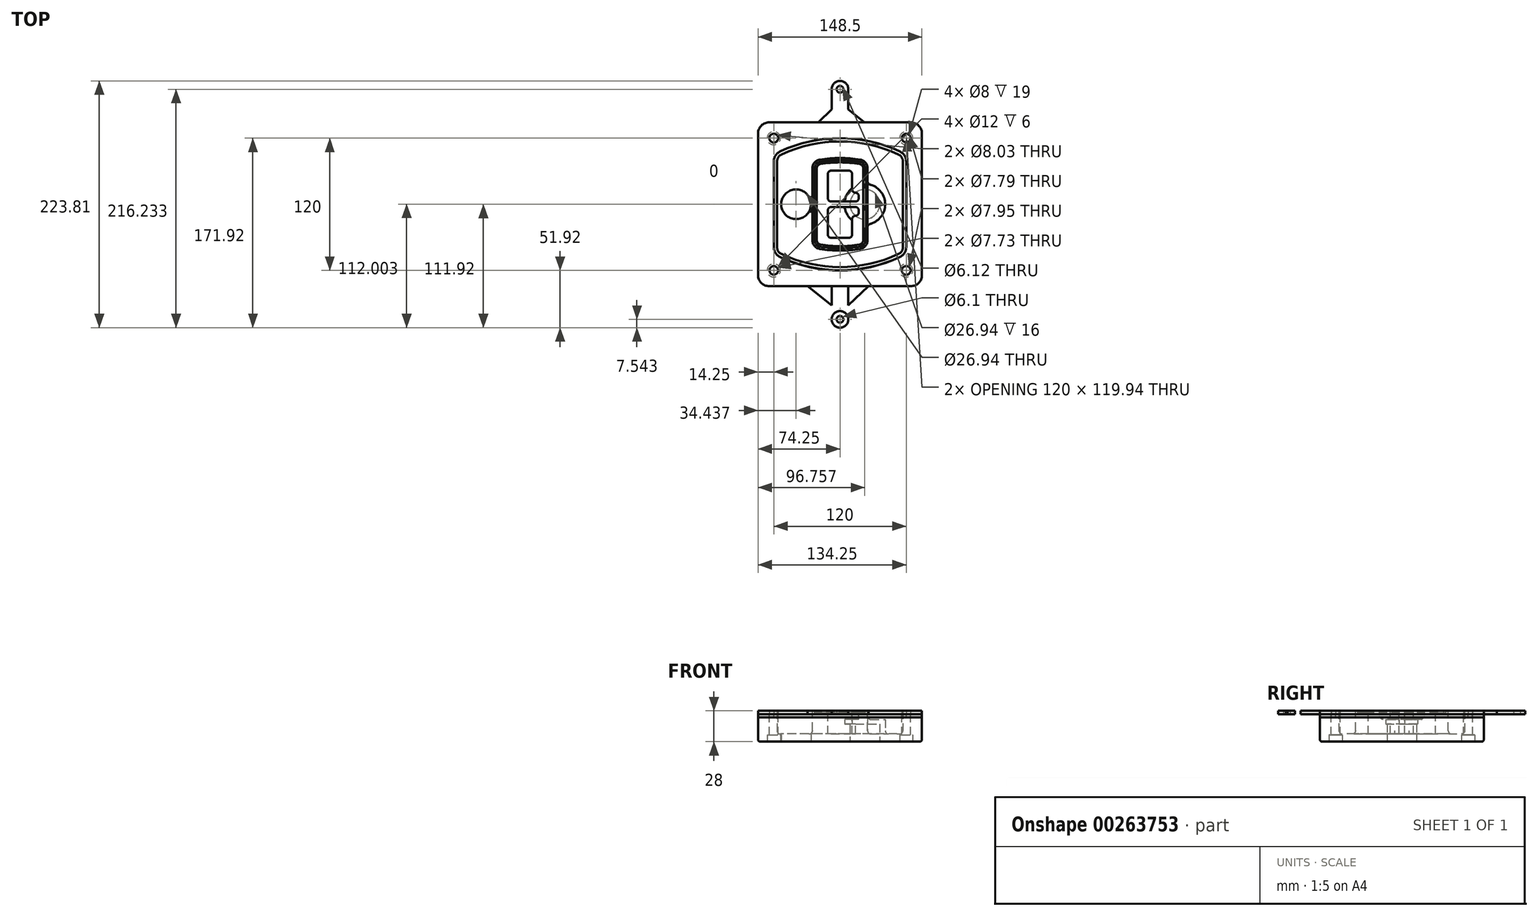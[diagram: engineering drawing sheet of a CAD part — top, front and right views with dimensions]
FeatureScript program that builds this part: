
annotation { "Feature Type Name" : "Feature", "Feature Type Description" : "" }
export const myFeature = defineFeature(function(context is Context, id is Id, definition is map)
    precondition{}
    {
        {
            var Q0;
            Q0=qCreatedBy(makeId("Top.planeOp"),FACE);
            var sketch = newSketch(context, id + "F0", { "sketchPlane" : qUnion([Q0])});
            skPoint(sketch, "E0.rect.middle", {"position": v(0, 0) * mm});
            skLineSegment(sketch, "E1.bottom", {"start": v(-64.25, -74.25) * mm, "end": v(64.25, -74.25) * mm});
            skLineSegment(sketch, "E1.top", {"start": v(-64.25, 74.25) * mm, "end": v(64.25, 74.25) * mm});
            skLineSegment(sketch, "E1.left", {"start": v(-74.25, -64.25) * mm, "end": v(-74.25, 64.25) * mm});
            skLineSegment(sketch, "E1.right", {"start": v(74.25, -64.25) * mm, "end": v(74.25, 64.25) * mm});
            skLineSegment(sketch, "E2", {"start": v(-74.25, 74.25) * mm, "end": v(74.25, -74.25) * mm, "construction": true});
            skLineSegment(sketch, "E3", {"start": v(74.25, 74.25) * mm, "end": v(-74.25, -74.25) * mm, "construction": true});
            skCircle(sketch, "E4", {"center": v(-60, 60) * mm, "radius": 4 * mm});
            skCircle(sketch, "E5", {"center": v(60, 60) * mm, "radius": 4 * mm});
            skCircle(sketch, "E6", {"center": v(60, -60) * mm, "radius": 4 * mm});
            skCircle(sketch, "E7", {"center": v(-60, -60) * mm, "radius": 4 * mm});
            skLineSegment(sketch, "E8", {"start": v(-60, 60) * mm, "end": v(60, 60) * mm, "construction": true});
            skLineSegment(sketch, "E9", {"start": v(60, 60) * mm, "end": v(60, -60) * mm, "construction": true});
            skLineSegment(sketch, "E10", {"start": v(60, -60) * mm, "end": v(-60, -60) * mm, "construction": true});
            skLineSegment(sketch, "E11", {"start": v(-60, -60) * mm, "end": v(-60, 60) * mm, "construction": true});
            skLineSegment(sketch, "E12", {"start": v(-60, 38.83) * mm, "end": v(-60, -38.83) * mm});
            skLineSegment(sketch, "E13", {"start": v(60, 38.83) * mm, "end": v(60, -38.83) * mm});
            skArc(sketch, "E14", {"start": v(54.26, 47.88) * mm, "mid": v(0, 60) * mm, "end": v(-54.26, 47.88) * mm});
            skArc(sketch, "E15", {"start": v(-54.26, -47.88) * mm, "mid": v(0, -60) * mm, "end": v(54.26, -47.88) * mm});
            skLineSegment(sketch, "E16", {"start": v(-60, 0) * mm, "end": v(60, 0) * mm, "construction": true});
            skPoint(sketch, "E17.visualSharp", {"position": v(-60, -45) * mm});
            skArc(sketch, "E17.filletArc", {"start": v(-60, -38.83) * mm, "mid": v(-58.44, -44.2) * mm, "end": v(-54.26, -47.88) * mm});
            skPoint(sketch, "E18.visualSharp", {"position": v(-60, 45) * mm});
            skArc(sketch, "E18.filletArc", {"start": v(-54.26, 47.88) * mm, "mid": v(-58.44, 44.2) * mm, "end": v(-60, 38.83) * mm});
            skPoint(sketch, "E19.visualSharp", {"position": v(60, 45) * mm});
            skArc(sketch, "E19.filletArc", {"start": v(60, 38.83) * mm, "mid": v(58.44, 44.2) * mm, "end": v(54.26, 47.88) * mm});
            skPoint(sketch, "E20.visualSharp", {"position": v(60, -45) * mm});
            skArc(sketch, "E20.filletArc", {"start": v(54.26, -47.88) * mm, "mid": v(58.44, -44.2) * mm, "end": v(60, -38.83) * mm});
            skPoint(sketch, "E21.visualSharp", {"position": v(-74.25, 74.25) * mm});
            skArc(sketch, "E21.filletArc", {"start": v(-64.25, 74.25) * mm, "mid": v(-71.32, 71.32) * mm, "end": v(-74.25, 64.25) * mm});
            skPoint(sketch, "E22.visualSharp", {"position": v(74.25, 74.25) * mm});
            skArc(sketch, "E22.filletArc", {"start": v(74.25, 64.25) * mm, "mid": v(71.32, 71.32) * mm, "end": v(64.25, 74.25) * mm});
            skPoint(sketch, "E23.visualSharp", {"position": v(74.25, -74.25) * mm});
            skArc(sketch, "E23.filletArc", {"start": v(64.25, -74.25) * mm, "mid": v(71.32, -71.32) * mm, "end": v(74.25, -64.25) * mm});
            skPoint(sketch, "E24.visualSharp", {"position": v(-74.25, -74.25) * mm});
            skArc(sketch, "E24.filletArc", {"start": v(-74.25, -64.25) * mm, "mid": v(-71.32, -71.32) * mm, "end": v(-64.25, -74.25) * mm});
            skArc(sketch, "E25.0", {"start": v(57, 38.83) * mm, "mid": v(55.9, 42.58) * mm, "end": v(52.98, 45.17) * mm});
            skLineSegment(sketch, "E25.1", {"start": v(57, 38.83) * mm, "end": v(57, -38.83) * mm});
            skArc(sketch, "E25.2", {"start": v(52.98, -45.17) * mm, "mid": v(55.9, -42.58) * mm, "end": v(57, -38.83) * mm});
            skArc(sketch, "E25.3", {"start": v(-52.98, -45.17) * mm, "mid": v(0, -57) * mm, "end": v(52.98, -45.17) * mm});
            skArc(sketch, "E25.4", {"start": v(-57, -38.83) * mm, "mid": v(-55.9, -42.58) * mm, "end": v(-52.98, -45.17) * mm});
            skArc(sketch, "E25.5", {"start": v(52.98, 45.17) * mm, "mid": v(0, 57) * mm, "end": v(-52.98, 45.17) * mm});
            skLineSegment(sketch, "E25.6", {"start": v(-57, 38.83) * mm, "end": v(-57, -38.83) * mm});
            skArc(sketch, "E25.7", {"start": v(-52.98, 45.17) * mm, "mid": v(-55.9, 42.58) * mm, "end": v(-57, 38.83) * mm});
            skArc(sketch, "E26.0", {"start": v(-55.96, 51.5) * mm, "mid": v(-61.82, 46.33) * mm, "end": v(-64, 38.83) * mm});
            skArc(sketch, "E26.1", {"start": v(55.96, 51.5) * mm, "mid": v(0, 64) * mm, "end": v(-55.96, 51.5) * mm});
            skArc(sketch, "E26.2", {"start": v(64, 38.83) * mm, "mid": v(61.82, 46.33) * mm, "end": v(55.96, 51.5) * mm});
            skLineSegment(sketch, "E26.3", {"start": v(64, 38.83) * mm, "end": v(64, -38.83) * mm});
            skArc(sketch, "E26.4", {"start": v(55.96, -51.5) * mm, "mid": v(61.82, -46.33) * mm, "end": v(64, -38.83) * mm});
            skLineSegment(sketch, "E26.5", {"start": v(-64, 38.83) * mm, "end": v(-64, -38.83) * mm});
            skArc(sketch, "E26.6", {"start": v(-55.96, -51.5) * mm, "mid": v(0, -64) * mm, "end": v(55.96, -51.5) * mm});
            skArc(sketch, "E26.7", {"start": v(-64, -38.83) * mm, "mid": v(-61.82, -46.33) * mm, "end": v(-55.96, -51.5) * mm});
            skSolve(sketch);
        }
        {
            var Q0;
            Q0=makeQuery(id+"F0.imprint","IMPRINT",FACE,{"disambiguationData":[TD([[makeQuery(id+"F0.imprint","IMPRINT",EDGE,{"derivedFrom":sQuery(id+"F0.wireOp",EDGE,"E1.bottom")}),1.0]])]});
            var Q1;
            Q1=makeQuery(id+"F0.imprint","IMPRINT",FACE,{"disambiguationData":[TD([[makeQuery(id+"F0.imprint","IMPRINT",EDGE,{"derivedFrom":sQuery(id+"F0.wireOp",EDGE,"E12")}),1.0]])]});
            var Q2;
            Q2=makeQuery(id+"F0.imprint","IMPRINT",FACE,{"disambiguationData":[TD([[makeQuery(id+"F0.imprint","IMPRINT",EDGE,{"derivedFrom":sQuery(id+"F0.wireOp",EDGE,"E25.0")}),1.0]])]});
            var Q3;
            Q3=makeQuery(id+"F0.imprint","IMPRINT",FACE,{"disambiguationData":[TD([[makeQuery(id+"F0.imprint","IMPRINT",EDGE,{"derivedFrom":sQuery(id+"F0.wireOp",EDGE,"E12")}),-1.0]])]});
            extrude(context, id + "F1", {"entities" : qUnion([Q0, Q1, Q2, Q3]), "oppositeDirection" : true, "depth" : 25 * mm});
        }
        {
            var Q0;
            Q0=makeQuery(id+"F0.imprint","IMPRINT",FACE,{"disambiguationData":[TD([[makeQuery(id+"F0.imprint","IMPRINT",EDGE,{"derivedFrom":sQuery(id+"F0.wireOp",EDGE,"E12")}),1.0]])]});
            extrude(context, id + "F2", {"entities" : qUnion([Q0]), "operationType" : NewBodyOperationType.ADD, "depth" : 3 * mm});
        }
        {
            var Q0;
            Q0=makeQuery(id+"F0.imprint","IMPRINT",FACE,{"disambiguationData":[TD([[makeQuery(id+"F0.imprint","IMPRINT",EDGE,{"derivedFrom":sQuery(id+"F0.wireOp",EDGE,"E25.0")}),1.0]])]});
            extrude(context, id + "F3", {"entities" : qUnion([Q0]), "operationType" : NewBodyOperationType.REMOVE, "oppositeDirection" : true, "depth" : 18 * mm});
        }
        {
            var Q0;
            Q0=makeQuery(id+"F2.opExtrude","CAP_FACE",FACE,{"disambiguationData":[OSD([sQuery(id+"F0.wireOp",EDGE,"E12"),sQuery(id+"F0.wireOp",EDGE,"E13"),sQuery(id+"F0.wireOp",EDGE,"E14"),sQuery(id+"F0.wireOp",EDGE,"E15"),sQuery(id+"F0.wireOp",EDGE,"E17.filletArc"),sQuery(id+"F0.wireOp",EDGE,"E18.filletArc"),sQuery(id+"F0.wireOp",EDGE,"E19.filletArc"),sQuery(id+"F0.wireOp",EDGE,"E20.filletArc"),sQuery(id+"F0.wireOp",EDGE,"E25.0"),sQuery(id+"F0.wireOp",EDGE,"E25.1"),sQuery(id+"F0.wireOp",EDGE,"E25.2"),sQuery(id+"F0.wireOp",EDGE,"E25.3"),sQuery(id+"F0.wireOp",EDGE,"E25.4"),sQuery(id+"F0.wireOp",EDGE,"E25.5"),sQuery(id+"F0.wireOp",EDGE,"E25.6"),sQuery(id+"F0.wireOp",EDGE,"E25.7")])],"isStart":false});
            var sketch = newSketch(context, id + "F4", { "sketchPlane" : qUnion([Q0])});
            skArc(sketch, "E27.0", {"start": v(-18.34, -40.45) * mm, "mid": v(0, -42) * mm, "end": v(18.34, -40.45) * mm});
            skArc(sketch, "E28.0", {"start": v(18.34, 40.45) * mm, "mid": v(0, 42) * mm, "end": v(-18.34, 40.45) * mm});
            skLineSegment(sketch, "E29", {"start": v(-25, 32.57) * mm, "end": v(-25, -32.57) * mm});
            skLineSegment(sketch, "E30", {"start": v(25, 32.57) * mm, "end": v(25, -32.57) * mm});
            skLineSegment(sketch, "E31", {"start": v(-25, 39.1) * mm, "end": v(25, 39.1) * mm, "construction": true});
            skLineSegment(sketch, "E32", {"start": v(-25, -39.1) * mm, "end": v(25, -39.1) * mm, "construction": true});
            skPoint(sketch, "E33.visualSharp", {"position": v(-25, 39.1) * mm});
            skArc(sketch, "E33.filletArc", {"start": v(-18.34, 40.45) * mm, "mid": v(-23.11, 37.73) * mm, "end": v(-25, 32.57) * mm});
            skPoint(sketch, "E34.visualSharp", {"position": v(25, 39.1) * mm});
            skArc(sketch, "E34.filletArc", {"start": v(25, 32.57) * mm, "mid": v(23.11, 37.73) * mm, "end": v(18.34, 40.45) * mm});
            skPoint(sketch, "E35.visualSharp", {"position": v(25, -39.1) * mm});
            skArc(sketch, "E35.filletArc", {"start": v(18.34, -40.45) * mm, "mid": v(23.11, -37.73) * mm, "end": v(25, -32.57) * mm});
            skPoint(sketch, "E36.visualSharp", {"position": v(-25, -39.1) * mm});
            skArc(sketch, "E36.filletArc", {"start": v(-25, -32.57) * mm, "mid": v(-23.11, -37.73) * mm, "end": v(-18.34, -40.45) * mm});
            skArc(sketch, "E37.0", {"start": v(52.98, 45.17) * mm, "mid": v(0, 57) * mm, "end": v(-52.98, 45.17) * mm});
            skArc(sketch, "E37.1", {"start": v(-52.98, 45.17) * mm, "mid": v(-55.9, 42.58) * mm, "end": v(-57, 38.83) * mm});
            skLineSegment(sketch, "E37.2", {"start": v(-57, 38.83) * mm, "end": v(-57, -38.83) * mm});
            skArc(sketch, "E37.3", {"start": v(-57, -38.83) * mm, "mid": v(-55.9, -42.58) * mm, "end": v(-52.98, -45.17) * mm});
            skArc(sketch, "E37.4", {"start": v(-52.98, -45.17) * mm, "mid": v(0, -57) * mm, "end": v(52.98, -45.17) * mm});
            skArc(sketch, "E37.5", {"start": v(52.98, -45.17) * mm, "mid": v(55.9, -42.58) * mm, "end": v(57, -38.83) * mm});
            skLineSegment(sketch, "E37.6", {"start": v(57, 38.83) * mm, "end": v(57, -38.83) * mm});
            skArc(sketch, "E37.7", {"start": v(57, 38.83) * mm, "mid": v(55.9, 42.58) * mm, "end": v(52.98, 45.17) * mm});
            skLineSegment(sketch, "E38.0", {"start": v(23, 32.57) * mm, "end": v(23, -32.57) * mm});
            skArc(sketch, "E38.1", {"start": v(18, -38.48) * mm, "mid": v(21.58, -36.44) * mm, "end": v(23, -32.57) * mm});
            skArc(sketch, "E38.2", {"start": v(-18, -38.48) * mm, "mid": v(0, -40) * mm, "end": v(18, -38.48) * mm});
            skArc(sketch, "E38.3", {"start": v(-23, -32.57) * mm, "mid": v(-21.58, -36.44) * mm, "end": v(-18, -38.48) * mm});
            skLineSegment(sketch, "E38.4", {"start": v(-23, 32.57) * mm, "end": v(-23, -32.57) * mm});
            skArc(sketch, "E38.5", {"start": v(23, 32.57) * mm, "mid": v(21.58, 36.44) * mm, "end": v(18, 38.48) * mm});
            skArc(sketch, "E38.6", {"start": v(-18, 38.48) * mm, "mid": v(-21.58, 36.44) * mm, "end": v(-23, 32.57) * mm});
            skArc(sketch, "E38.7", {"start": v(18, 38.48) * mm, "mid": v(0, 40) * mm, "end": v(-18, 38.48) * mm});
            skArc(sketch, "E39.0", {"start": v(21, 32.57) * mm, "mid": v(20.06, 35.15) * mm, "end": v(17.67, 36.5) * mm});
            skLineSegment(sketch, "E39.1", {"start": v(21, 32.57) * mm, "end": v(21, -32.57) * mm});
            skArc(sketch, "E39.2", {"start": v(17.67, -36.5) * mm, "mid": v(20.06, -35.15) * mm, "end": v(21, -32.57) * mm});
            skArc(sketch, "E39.3", {"start": v(-17.67, -36.5) * mm, "mid": v(0, -38) * mm, "end": v(17.67, -36.5) * mm});
            skArc(sketch, "E39.4", {"start": v(-21, -32.57) * mm, "mid": v(-20.06, -35.15) * mm, "end": v(-17.67, -36.5) * mm});
            skArc(sketch, "E39.5", {"start": v(17.67, 36.5) * mm, "mid": v(0, 38) * mm, "end": v(-17.67, 36.5) * mm});
            skLineSegment(sketch, "E39.6", {"start": v(-21, 32.57) * mm, "end": v(-21, -32.57) * mm});
            skArc(sketch, "E39.7", {"start": v(-17.67, 36.5) * mm, "mid": v(-20.06, 35.15) * mm, "end": v(-21, 32.57) * mm});
            skLineSegment(sketch, "E40", {"start": v(-25, 0) * mm, "end": v(25, 0) * mm, "construction": true});
            skLineSegment(sketch, "E41", {"start": v(-11, 5.5) * mm, "end": v(-11, 27.5) * mm});
            skLineSegment(sketch, "E42", {"start": v(-8, 30.5) * mm, "end": v(8, 30.5) * mm});
            skLineSegment(sketch, "E43", {"start": v(11, 27.5) * mm, "end": v(11, 13.5) * mm});
            skLineSegment(sketch, "E44", {"start": v(14, 10.5) * mm, "end": v(14, 10.5) * mm});
            skLineSegment(sketch, "E45", {"start": v(17, 7.5) * mm, "end": v(17, 5.5) * mm});
            skLineSegment(sketch, "E46", {"start": v(14, 2.5) * mm, "end": v(-8, 2.5) * mm});
            skPoint(sketch, "E47.visualSharp", {"position": v(-11, 30.5) * mm});
            skArc(sketch, "E47.filletArc", {"start": v(-8, 30.5) * mm, "mid": v(-10.12, 29.62) * mm, "end": v(-11, 27.5) * mm});
            skPoint(sketch, "E48.visualSharp", {"position": v(11, 30.5) * mm});
            skArc(sketch, "E48.filletArc", {"start": v(11, 27.5) * mm, "mid": v(10.12, 29.62) * mm, "end": v(8, 30.5) * mm});
            skPoint(sketch, "E49.visualSharp", {"position": v(11, 10.5) * mm});
            skArc(sketch, "E49.filletArc", {"start": v(11, 13.5) * mm, "mid": v(11.88, 11.38) * mm, "end": v(14, 10.5) * mm});
            skPoint(sketch, "E50.visualSharp", {"position": v(17, 10.5) * mm});
            skArc(sketch, "E50.filletArc", {"start": v(17, 7.5) * mm, "mid": v(16.12, 9.62) * mm, "end": v(14, 10.5) * mm});
            skPoint(sketch, "E51.visualSharp", {"position": v(17, 2.5) * mm});
            skArc(sketch, "E51.filletArc", {"start": v(14, 2.5) * mm, "mid": v(16.12, 3.38) * mm, "end": v(17, 5.5) * mm});
            skPoint(sketch, "E52.visualSharp", {"position": v(-11, 2.5) * mm});
            skArc(sketch, "E52.filletArc", {"start": v(-11, 5.5) * mm, "mid": v(-10.12, 3.38) * mm, "end": v(-8, 2.5) * mm});
            skLineSegment(sketch, "E53.0.MirrorCS", {"start": v(14, -2.5) * mm, "end": v(-8, -2.5) * mm});
            skArc(sketch, "E54.0.MirrorCS", {"start": v(-11, -5.5) * mm, "mid": v(-10.12, -3.38) * mm, "end": v(-8, -2.5) * mm});
            skLineSegment(sketch, "E55.0.MirrorCS", {"start": v(-11, -5.5) * mm, "end": v(-11, -27.5) * mm});
            skArc(sketch, "E56.0.MirrorCS", {"start": v(-8, -30.5) * mm, "mid": v(-10.12, -29.62) * mm, "end": v(-11, -27.5) * mm});
            skLineSegment(sketch, "E57.0.MirrorCS", {"start": v(-8, -30.5) * mm, "end": v(8, -30.5) * mm});
            skArc(sketch, "E58.0.MirrorCS", {"start": v(11, -27.5) * mm, "mid": v(10.12, -29.62) * mm, "end": v(8, -30.5) * mm});
            skLineSegment(sketch, "E59.0.MirrorCS", {"start": v(11, -27.5) * mm, "end": v(11, -13.5) * mm});
            skArc(sketch, "E60.0.MirrorCS", {"start": v(11, -13.5) * mm, "mid": v(11.88, -11.38) * mm, "end": v(14, -10.5) * mm});
            skArc(sketch, "E61.0.MirrorCS", {"start": v(17, -7.5) * mm, "mid": v(16.12, -9.62) * mm, "end": v(14, -10.5) * mm});
            skLineSegment(sketch, "E62.0.MirrorCS", {"start": v(17, -7.5) * mm, "end": v(17, -5.5) * mm});
            skArc(sketch, "E63.0.MirrorCS", {"start": v(14, -2.5) * mm, "mid": v(16.12, -3.38) * mm, "end": v(17, -5.5) * mm});
            skSolve(sketch);
        }
        {
            var Q0;
            Q0=makeQuery(id+"F4.imprint","IMPRINT",FACE,{"disambiguationData":[TD([[makeQuery(id+"F4.imprint","IMPRINT",EDGE,{"derivedFrom":sQuery(id+"F4.wireOp",EDGE,"E27.0")}),1.0]])]});
            var Q1;
            Q1=makeQuery(id+"F4.imprint","IMPRINT",FACE,{"disambiguationData":[TD([[makeQuery(id+"F4.imprint","IMPRINT",EDGE,{"derivedFrom":sQuery(id+"F4.wireOp",EDGE,"E38.0")}),-1.0]])]});
            var Q2;
            Q2=makeQuery(id+"F4.imprint","IMPRINT",FACE,{"disambiguationData":[TD([[makeQuery(id+"F4.imprint","IMPRINT",EDGE,{"derivedFrom":sQuery(id+"F4.wireOp",EDGE,"E39.0")}),1.0]])]});
            extrude(context, id + "F5", {"entities" : qUnion([Q0, Q1, Q2]), "operationType" : NewBodyOperationType.ADD, "endBound" : BoundingType.UP_TO_NEXT, "oppositeDirection" : true, "depth" : 25 * mm});
        }
        {
            var Q0;
            Q0=makeQuery(id+"F4.imprint","IMPRINT",FACE,{"disambiguationData":[TD([[makeQuery(id+"F4.imprint","IMPRINT",EDGE,{"derivedFrom":sQuery(id+"F4.wireOp",EDGE,"E38.0")}),-1.0]])]});
            extrude(context, id + "F6", {"entities" : qUnion([Q0]), "operationType" : NewBodyOperationType.REMOVE, "oppositeDirection" : true, "depth" : 2 * mm});
        }
        {
            var Q0;
            Q0=makeQuery(id+"F1.opExtrude","CAP_FACE",FACE,{"disambiguationData":[OSD([sQuery(id+"F0.wireOp",EDGE,"E1.bottom"),sQuery(id+"F0.wireOp",EDGE,"E1.top"),sQuery(id+"F0.wireOp",EDGE,"E1.left"),sQuery(id+"F0.wireOp",EDGE,"E1.right"),sQuery(id+"F0.wireOp",EDGE,"E4"),sQuery(id+"F0.wireOp",EDGE,"E5"),sQuery(id+"F0.wireOp",EDGE,"E6"),sQuery(id+"F0.wireOp",EDGE,"E7"),sQuery(id+"F0.wireOp",EDGE,"E21.filletArc"),sQuery(id+"F0.wireOp",EDGE,"E22.filletArc"),sQuery(id+"F0.wireOp",EDGE,"E23.filletArc"),sQuery(id+"F0.wireOp",EDGE,"E24.filletArc")])],"isStart":false});
            var sketch = newSketch(context, id + "F7", { "sketchPlane" : qUnion([Q0])});
            skCircle(sketch, "E64", {"center": v(22.5, 0) * mm, "radius": 13.47 * mm});
            skCircle(sketch, "E65", {"center": v(-39.81, 0) * mm, "radius": 13.47 * mm});
            skLineSegment(sketch, "E66", {"start": v(74.25, 0) * mm, "end": v(-74.25, 0) * mm});
            skCircle(sketch, "E67", {"center": v(22.5, 0) * mm, "radius": 18.47 * mm});
            skCircle(sketch, "E68", {"center": v(60, -60) * mm, "radius": 6 * mm});
            skCircle(sketch, "E69", {"center": v(-60, -60) * mm, "radius": 6 * mm});
            skCircle(sketch, "E70", {"center": v(-60, 60) * mm, "radius": 6 * mm});
            skCircle(sketch, "E71", {"center": v(60, 60) * mm, "radius": 6 * mm});
            skSolve(sketch);
        }
        {
            var Q0;
            {var subQ1=sQuery(id+"F7.wireOp",EDGE,"E66");var subQ4=sQuery(id+"F7.wireOp",EDGE,"E64");var subQ6=makeQuery(id+"F7.imprint","INTERSECT",VERTEX,{"disambiguationData":[OD(0.0)],"derivedFrom":[subQ4,subQ1]});Q0=makeQuery(id+"F7.imprint","IMPRINT",FACE,{"disambiguationData":[TD([[makeQuery(id+"F7.imprint","IMPRINT",EDGE,{"disambiguationData":[TD([[subQ6,-1.0]])],"derivedFrom":subQ4}),-1.0]])]});}
            var Q1;
            {var subQ0=sQuery(id+"F7.wireOp",EDGE,"E66");var subQ1=sQuery(id+"F7.wireOp",EDGE,"E64");var subQ3=makeQuery(id+"F7.imprint","INTERSECT",VERTEX,{"disambiguationData":[OD(0.0)],"derivedFrom":[subQ1,subQ0]});Q1=makeQuery(id+"F7.imprint","IMPRINT",FACE,{"disambiguationData":[TD([[makeQuery(id+"F7.imprint","IMPRINT",EDGE,{"disambiguationData":[TD([[subQ3,-1.0]])],"derivedFrom":subQ1}),1.0]])]});}
            var Q2;
            {var subQ0=sQuery(id+"F7.wireOp",EDGE,"E66");var subQ1=sQuery(id+"F7.wireOp",EDGE,"E64");var subQ3=makeQuery(id+"F7.imprint","INTERSECT",VERTEX,{"disambiguationData":[OD(0.0)],"derivedFrom":[subQ1,subQ0]});Q2=makeQuery(id+"F7.imprint","IMPRINT",FACE,{"disambiguationData":[TD([[makeQuery(id+"F7.imprint","IMPRINT",EDGE,{"disambiguationData":[TD([[subQ3,1.0]])],"derivedFrom":subQ1}),1.0]])]});}
            var Q3;
            {var subQ1=sQuery(id+"F7.wireOp",EDGE,"E66");var subQ4=sQuery(id+"F7.wireOp",EDGE,"E64");var subQ6=makeQuery(id+"F7.imprint","INTERSECT",VERTEX,{"disambiguationData":[OD(0.0)],"derivedFrom":[subQ4,subQ1]});Q3=makeQuery(id+"F7.imprint","IMPRINT",FACE,{"disambiguationData":[TD([[makeQuery(id+"F7.imprint","IMPRINT",EDGE,{"disambiguationData":[TD([[subQ6,1.0]])],"derivedFrom":subQ4}),-1.0]])]});}
            extrude(context, id + "F8", {"entities" : qUnion([Q0, Q1, Q2, Q3]), "operationType" : NewBodyOperationType.ADD, "oppositeDirection" : true, "depth" : 20 * mm});
        }
        {
            var Q0;
            {var subQ0=sQuery(id+"F7.wireOp",EDGE,"E66");var subQ1=sQuery(id+"F7.wireOp",EDGE,"E64");var subQ3=makeQuery(id+"F7.imprint","INTERSECT",VERTEX,{"disambiguationData":[OD(0.0)],"derivedFrom":[subQ1,subQ0]});Q0=makeQuery(id+"F7.imprint","IMPRINT",FACE,{"disambiguationData":[TD([[makeQuery(id+"F7.imprint","IMPRINT",EDGE,{"disambiguationData":[TD([[subQ3,-1.0]])],"derivedFrom":subQ1}),1.0]])]});}
            var Q1;
            {var subQ0=sQuery(id+"F7.wireOp",EDGE,"E66");var subQ1=sQuery(id+"F7.wireOp",EDGE,"E64");var subQ3=makeQuery(id+"F7.imprint","INTERSECT",VERTEX,{"disambiguationData":[OD(0.0)],"derivedFrom":[subQ1,subQ0]});Q1=makeQuery(id+"F7.imprint","IMPRINT",FACE,{"disambiguationData":[TD([[makeQuery(id+"F7.imprint","IMPRINT",EDGE,{"disambiguationData":[TD([[subQ3,1.0]])],"derivedFrom":subQ1}),1.0]])]});}
            extrude(context, id + "F9", {"entities" : qUnion([Q0, Q1]), "operationType" : NewBodyOperationType.REMOVE, "oppositeDirection" : true, "depth" : 16 * mm});
        }
        {
            var Q0;
            {var subQ0=sQuery(id+"F7.wireOp",EDGE,"E66");var subQ1=sQuery(id+"F7.wireOp",EDGE,"E65");var subQ3=makeQuery(id+"F7.imprint","INTERSECT",VERTEX,{"disambiguationData":[OD(0.0)],"derivedFrom":[subQ1,subQ0]});Q0=makeQuery(id+"F7.imprint","IMPRINT",FACE,{"disambiguationData":[TD([[makeQuery(id+"F7.imprint","IMPRINT",EDGE,{"disambiguationData":[TD([[subQ3,-1.0]])],"derivedFrom":subQ1}),1.0]])]});}
            var Q1;
            {var subQ0=sQuery(id+"F7.wireOp",EDGE,"E66");var subQ1=sQuery(id+"F7.wireOp",EDGE,"E65");var subQ3=makeQuery(id+"F7.imprint","INTERSECT",VERTEX,{"disambiguationData":[OD(0.0)],"derivedFrom":[subQ1,subQ0]});Q1=makeQuery(id+"F7.imprint","IMPRINT",FACE,{"disambiguationData":[TD([[makeQuery(id+"F7.imprint","IMPRINT",EDGE,{"disambiguationData":[TD([[subQ3,1.0]])],"derivedFrom":subQ1}),1.0]])]});}
            extrude(context, id + "F10", {"entities" : qUnion([Q0, Q1]), "operationType" : NewBodyOperationType.REMOVE, "oppositeDirection" : true, "depth" : 25 * mm});
        }
        {
            var Q0;
            Q0=makeQuery(id+"F7.imprint","IMPRINT",FACE,{"disambiguationData":[TD([[makeQuery(id+"F7.imprint","IMPRINT",EDGE,{"derivedFrom":sQuery(id+"F7.wireOp",EDGE,"E68")}),1.0]])]});
            var Q1;
            Q1=makeQuery(id+"F7.imprint","IMPRINT",FACE,{"disambiguationData":[TD([[makeQuery(id+"F7.imprint","IMPRINT",EDGE,{"derivedFrom":makeQuery(id+"F1.opExtrude","CAP_EDGE",EDGE,{"disambiguationData":[OSD([sQuery(id+"F0.wireOp",EDGE,"E5")])],"isStart":false})}),-1.0]])]});
            var Q2;
            Q2=makeQuery(id+"F7.imprint","IMPRINT",FACE,{"disambiguationData":[TD([[makeQuery(id+"F7.imprint","IMPRINT",EDGE,{"derivedFrom":sQuery(id+"F7.wireOp",EDGE,"E69")}),1.0]])]});
            var Q3;
            Q3=makeQuery(id+"F7.imprint","IMPRINT",FACE,{"disambiguationData":[TD([[makeQuery(id+"F7.imprint","IMPRINT",EDGE,{"derivedFrom":makeQuery(id+"F1.opExtrude","CAP_EDGE",EDGE,{"disambiguationData":[OSD([sQuery(id+"F0.wireOp",EDGE,"E4")])],"isStart":false})}),-1.0]])]});
            var Q4;
            Q4=makeQuery(id+"F7.imprint","IMPRINT",FACE,{"disambiguationData":[TD([[makeQuery(id+"F7.imprint","IMPRINT",EDGE,{"derivedFrom":sQuery(id+"F7.wireOp",EDGE,"E70")}),1.0]])]});
            var Q5;
            Q5=makeQuery(id+"F7.imprint","IMPRINT",FACE,{"disambiguationData":[TD([[makeQuery(id+"F7.imprint","IMPRINT",EDGE,{"derivedFrom":makeQuery(id+"F1.opExtrude","CAP_EDGE",EDGE,{"disambiguationData":[OSD([sQuery(id+"F0.wireOp",EDGE,"E7")])],"isStart":false})}),-1.0]])]});
            var Q6;
            Q6=makeQuery(id+"F7.imprint","IMPRINT",FACE,{"disambiguationData":[TD([[makeQuery(id+"F7.imprint","IMPRINT",EDGE,{"derivedFrom":sQuery(id+"F7.wireOp",EDGE,"E71")}),1.0]])]});
            var Q7;
            Q7=makeQuery(id+"F7.imprint","IMPRINT",FACE,{"disambiguationData":[TD([[makeQuery(id+"F7.imprint","IMPRINT",EDGE,{"derivedFrom":makeQuery(id+"F1.opExtrude","CAP_EDGE",EDGE,{"disambiguationData":[OSD([sQuery(id+"F0.wireOp",EDGE,"E6")])],"isStart":false})}),-1.0]])]});
            extrude(context, id + "F11", {"entities" : qUnion([Q0, Q1, Q2, Q3, Q4, Q5, Q6, Q7]), "operationType" : NewBodyOperationType.REMOVE, "oppositeDirection" : true, "depth" : 6 * mm});
        }
        {
            var Q0;
            Q0=makeQuery(id+"F9.boolean.opBoolean","COPY",FACE,{"derivedFrom":makeQuery(id+"F9.opExtrude","CAP_FACE",FACE,{"disambiguationData":[OSD([sQuery(id+"F7.wireOp",EDGE,"E64")])],"isStart":false})});
            var sketch = newSketch(context, id + "F12", { "sketchPlane" : qUnion([Q0])});
            skArc(sketch, "E72.0", {"start": v(11, 14.45) * mm, "mid": v(6.45, 9.13) * mm, "end": v(4.2, 2.5) * mm});
            skArc(sketch, "E72.1", {"start": v(4.2, -2.5) * mm, "mid": v(6.45, -9.13) * mm, "end": v(11, -14.45) * mm});
            skLineSegment(sketch, "E73", {"start": v(4.2, -2.5) * mm, "end": v(14, -2.5) * mm});
            skLineSegment(sketch, "E74.0", {"start": v(14, 2.5) * mm, "end": v(4.2, 2.5) * mm});
            skArc(sketch, "E74.1", {"start": v(14, 2.5) * mm, "mid": v(16.12, 3.38) * mm, "end": v(17, 5.5) * mm});
            skLineSegment(sketch, "E74.2", {"start": v(17, 7.5) * mm, "end": v(17, 5.5) * mm});
            skArc(sketch, "E74.3", {"start": v(17, 7.5) * mm, "mid": v(16.12, 9.62) * mm, "end": v(14, 10.5) * mm});
            skArc(sketch, "E74.4", {"start": v(11, 13.5) * mm, "mid": v(11.88, 11.38) * mm, "end": v(14, 10.5) * mm});
            skLineSegment(sketch, "E74.5", {"start": v(11, 14.45) * mm, "end": v(11, 13.5) * mm});
            skLineSegment(sketch, "E74.7", {"start": v(14, -2.5) * mm, "end": v(4.2, -2.5) * mm});
            skArc(sketch, "E74.8", {"start": v(14, -2.5) * mm, "mid": v(16.12, -3.38) * mm, "end": v(17, -5.5) * mm});
            skLineSegment(sketch, "E74.9", {"start": v(17, -7.5) * mm, "end": v(17, -5.5) * mm});
            skArc(sketch, "E74.10", {"start": v(17, -7.5) * mm, "mid": v(16.12, -9.62) * mm, "end": v(14, -10.5) * mm});
            skArc(sketch, "E74.11", {"start": v(11, -13.5) * mm, "mid": v(11.88, -11.38) * mm, "end": v(14, -10.5) * mm});
            skLineSegment(sketch, "E74.12", {"start": v(11, -14.45) * mm, "end": v(11, -13.5) * mm});
            skPoint(sketch, "E75.orphan", {"position": v(11, -27.5) * mm});
            skPoint(sketch, "E76.orphan", {"position": v(-8, -2.5) * mm});
            skPoint(sketch, "E77.orphan", {"position": v(-8, 2.5) * mm});
            skPoint(sketch, "E78.orphan", {"position": v(11, 27.5) * mm});
            skSolve(sketch);
        }
        {
            var Q0;
            {var subQ7=sQuery(id+"F12.wireOp",EDGE,"E72.0");var subQ14=sQuery(id+"F12.wireOp",EDGE,"E72.1");var subQ16=sQuery(id+"F12.wireOp",EDGE,"E74.1");var subQ18=sQuery(id+"F12.wireOp",EDGE,"E74.8");Q0=qUnion([makeQuery(id+"F12.imprint","IMPRINT",FACE,{"disambiguationData":[TD([[makeQuery(id+"F12.imprint","IMPRINT",EDGE,{"derivedFrom":subQ7}),1.0]])]}),makeQuery(id+"F12.imprint","IMPRINT",FACE,{"disambiguationData":[TD([[makeQuery(id+"F12.imprint","IMPRINT",EDGE,{"derivedFrom":subQ14}),1.0]])]}),makeQuery(id+"F12.imprint","IMPRINT",FACE,{"disambiguationData":[TD([[makeQuery(id+"F12.imprint","IMPRINT",EDGE,{"derivedFrom":subQ16}),1.0]])]}),makeQuery(id+"F12.imprint","IMPRINT",FACE,{"disambiguationData":[TD([[makeQuery(id+"F12.imprint","IMPRINT",EDGE,{"derivedFrom":subQ18}),-1.0]])]})]);}
            var Q1;
            Q1=makeQuery(id+"F5.boolean.opBoolean","SPLIT",FACE,{"disambiguationData":[TD([makeQuery(id+"F5.opExtrude","SWEPT_FACE",FACE,{"disambiguationData":[OSD([sQuery(id+"F4.wireOp",EDGE,"E41")])]})])],"derivedFrom":makeQuery(id+"F3.boolean.opBoolean","COPY",FACE,{"derivedFrom":makeQuery(id+"F3.opExtrude","CAP_FACE",FACE,{"disambiguationData":[OSD([sQuery(id+"F0.wireOp",EDGE,"E25.0"),sQuery(id+"F0.wireOp",EDGE,"E25.1"),sQuery(id+"F0.wireOp",EDGE,"E25.2"),sQuery(id+"F0.wireOp",EDGE,"E25.3"),sQuery(id+"F0.wireOp",EDGE,"E25.4"),sQuery(id+"F0.wireOp",EDGE,"E25.5"),sQuery(id+"F0.wireOp",EDGE,"E25.6"),sQuery(id+"F0.wireOp",EDGE,"E25.7")])],"isStart":false})})});
            extrude(context, id + "F13", {"entities" : qUnion([Q0]), "operationType" : NewBodyOperationType.REMOVE, "endBound" : BoundingType.UP_TO_SURFACE, "endBoundEntityFace" : qUnion([Q1]), "depth" : 25 * mm});
        }
        {
            var Q0;
            Q0=makeQuery(id+"F3.boolean.opBoolean","COPY",EDGE,{"derivedFrom":makeQuery(id+"F3.opExtrude","CAP_EDGE",EDGE,{"disambiguationData":[OSD([sQuery(id+"F0.wireOp",EDGE,"E25.6")])],"isStart":false})});
            var Q1;
            Q1=makeQuery(id+"F8.boolean.opBoolean","INTERSECT",EDGE,{"derivedFrom":[makeQuery(id+"F5.opExtrude","SWEPT_FACE",FACE,{"disambiguationData":[OSD([sQuery(id+"F4.wireOp",EDGE,"E30")])]}),makeQuery(id+"F8.opExtrude","CAP_FACE",FACE,{"disambiguationData":[OSD([sQuery(id+"F7.wireOp",EDGE,"E67")])],"isStart":false})]});
            var Q2;
            Q2=makeQuery(id+"F8.boolean.opBoolean","INTERSECT",EDGE,{"disambiguationData":[OD(1.0)],"derivedFrom":[makeQuery(id+"F5.opExtrude","SWEPT_FACE",FACE,{"disambiguationData":[OSD([sQuery(id+"F4.wireOp",EDGE,"E30")])]}),makeQuery(id+"F8.opExtrude","SWEPT_FACE",FACE,{"disambiguationData":[OSD([sQuery(id+"F7.wireOp",EDGE,"E67")])]})]});
            var Q3;
            {var subQ0=sQuery(id+"F4.wireOp",EDGE,"E30");Q3=makeQuery(id+"F8.boolean.opBoolean","SPLIT",EDGE,{"disambiguationData":[TD([makeQuery(id+"F5.opExtrude","SWEPT_FACE",FACE,{"disambiguationData":[OSD([sQuery(id+"F4.wireOp",EDGE,"E35.filletArc")])]})])],"derivedFrom":makeQuery(id+"F5.opExtrude","CAP_EDGE",EDGE,{"disambiguationData":[OSD([subQ0])],"isStart":false})});}
            var Q4;
            {var subQ0=sQuery(id+"F0.wireOp",EDGE,"E25.7");var subQ1=sQuery(id+"F0.wireOp",EDGE,"E25.1");var subQ2=sQuery(id+"F0.wireOp",EDGE,"E25.6");var subQ3=sQuery(id+"F0.wireOp",EDGE,"E25.5");var subQ4=sQuery(id+"F0.wireOp",EDGE,"E25.4");var subQ5=sQuery(id+"F0.wireOp",EDGE,"E25.0");var subQ6=sQuery(id+"F0.wireOp",EDGE,"E25.2");var subQ7=sQuery(id+"F0.wireOp",EDGE,"E25.3");Q4=makeQuery(id+"F8.boolean.opBoolean","INTERSECT",EDGE,{"derivedFrom":[makeQuery(id+"F5.boolean.opBoolean","SPLIT",FACE,{"disambiguationData":[TD([makeQuery(id+"F2.opExtrude","SWEPT_FACE",FACE,{"disambiguationData":[OSD([subQ5])]})])],"derivedFrom":makeQuery(id+"F3.boolean.opBoolean","COPY",FACE,{"derivedFrom":makeQuery(id+"F3.opExtrude","CAP_FACE",FACE,{"disambiguationData":[OSD([subQ5,subQ1,subQ6,subQ7,subQ4,subQ3,subQ2,subQ0])],"isStart":false})})}),makeQuery(id+"F8.opExtrude","SWEPT_FACE",FACE,{"disambiguationData":[OSD([sQuery(id+"F7.wireOp",EDGE,"E67")])]})]});}
            var Q5;
            Q5=makeQuery(id+"F8.boolean.opBoolean","INTERSECT",EDGE,{"disambiguationData":[OD(0.0)],"derivedFrom":[makeQuery(id+"F5.opExtrude","SWEPT_FACE",FACE,{"disambiguationData":[OSD([sQuery(id+"F4.wireOp",EDGE,"E30")])]}),makeQuery(id+"F8.opExtrude","SWEPT_FACE",FACE,{"disambiguationData":[OSD([sQuery(id+"F7.wireOp",EDGE,"E67")])]})]});
            fillet(context, id + "F14", {"entities" : qUnion([Q0, Q1, Q2, Q3, Q4, Q5]), "radius" : 3 * mm, "tangentPropagation" : true, "allowEdgeOverflow" : false});
        }
        {
            var Q0;
            Q0=makeQuery(id+"F1.opExtrude","CAP_EDGE",EDGE,{"disambiguationData":[OSD([sQuery(id+"F0.wireOp",EDGE,"E1.bottom")])],"isStart":false});
            fillet(context, id + "F15", {"entities" : qUnion([Q0]), "radius" : 2 * mm, "tangentPropagation" : true, "allowEdgeOverflow" : false});
        }
        {
            var Q0;
            {var subQ0=sQuery(id+"F0.wireOp",EDGE,"E22.filletArc");var subQ1=sQuery(id+"F0.wireOp",EDGE,"E7");var subQ2=sQuery(id+"F0.wireOp",EDGE,"E6");var subQ3=sQuery(id+"F0.wireOp",EDGE,"E5");var subQ4=sQuery(id+"F0.wireOp",EDGE,"E4");var subQ5=sQuery(id+"F0.wireOp",EDGE,"E1.bottom");var subQ6=sQuery(id+"F0.wireOp",EDGE,"E21.filletArc");var subQ7=sQuery(id+"F0.wireOp",EDGE,"E1.top");var subQ8=sQuery(id+"F0.wireOp",EDGE,"E1.left");var subQ9=sQuery(id+"F0.wireOp",EDGE,"E1.right");var subQ10=sQuery(id+"F0.wireOp",EDGE,"E23.filletArc");var subQ11=sQuery(id+"F0.wireOp",EDGE,"E24.filletArc");Q0=makeQuery(id+"F2.boolean.opBoolean","SPLIT",FACE,{"disambiguationData":[TD([makeQuery(id+"F1.opExtrude","SWEPT_FACE",FACE,{"disambiguationData":[OSD([subQ5])]})])],"derivedFrom":makeQuery(id+"F1.opExtrude","CAP_FACE",FACE,{"disambiguationData":[OSD([subQ5,subQ7,subQ8,subQ9,subQ4,subQ3,subQ2,subQ1,subQ6,subQ0,subQ10,subQ11])],"isStart":true})});}
            var sketch = newSketch(context, id + "F16", { "sketchPlane" : qUnion([Q0])});
            skLineSegment(sketch, "E79", {"start": v(0, -74.25) * mm, "end": v(0, -104.38) * mm});
            skCircle(sketch, "E80", {"center": v(0, -104.38) * mm, "radius": 7.54 * mm});
            skLineSegment(sketch, "E81", {"start": v(-7.5, -105.15) * mm, "end": v(-7.5, -74.25) * mm});
            skLineSegment(sketch, "E82", {"start": v(7.5, -105.2) * mm, "end": v(7.5, -74.25) * mm});
            skCircle(sketch, "E83", {"center": v(0, -104.38) * mm, "radius": 3.05 * mm});
            skLineSegment(sketch, "E84", {"start": v(7.5, -74.25) * mm, "end": v(7.5, -91.63) * mm});
            skLineSegment(sketch, "E85", {"start": v(25.9, -74.25) * mm, "end": v(7.5, -91.63) * mm});
            skLineSegment(sketch, "E86", {"start": v(-7.5, -91.63) * mm, "end": v(-29.32, -74.25) * mm});
            skLineSegment(sketch, "E87", {"start": v(-29.32, -74.25) * mm, "end": v(25.9, -74.25) * mm});
            skLineSegment(sketch, "E88", {"start": v(25.9, -74.25) * mm, "end": v(-29.32, -74.25) * mm});
            skLineSegment(sketch, "E89", {"start": v(-7.5, -74.25) * mm, "end": v(-7.5, -91.63) * mm});
            skSolve(sketch);
        }
        {
            var Q0;
            {var subQ0=sQuery(id+"F16.wireOp",EDGE,"E85");Q0=makeQuery(id+"F16.imprint","IMPRINT",FACE,{"disambiguationData":[TD([[makeQuery(id+"F16.imprint","IMPRINT",EDGE,{"derivedFrom":subQ0}),-1.0]])]});}
            var Q1;
            {var subQ0=sQuery(id+"F16.wireOp",EDGE,"E86");Q1=makeQuery(id+"F16.imprint","IMPRINT",FACE,{"disambiguationData":[TD([[makeQuery(id+"F16.imprint","IMPRINT",EDGE,{"derivedFrom":subQ0}),-1.0]])]});}
            var Q2;
            {var subQ0=sQuery(id+"F16.wireOp",EDGE,"E84");Q2=makeQuery(id+"F16.imprint","IMPRINT",FACE,{"disambiguationData":[TD([[makeQuery(id+"F16.imprint","IMPRINT",EDGE,{"derivedFrom":subQ0}),-1.0]])]});}
            var Q3;
            {var subQ0=sQuery(id+"F16.wireOp",EDGE,"E89");Q3=makeQuery(id+"F16.imprint","IMPRINT",FACE,{"disambiguationData":[TD([[makeQuery(id+"F16.imprint","IMPRINT",EDGE,{"derivedFrom":subQ0}),1.0]])]});}
            var Q4;
            Q4=makeQuery(id+"F16.imprint","IMPRINT",FACE,{"disambiguationData":[TD([[makeQuery(id+"F16.imprint","IMPRINT",EDGE,{"derivedFrom":sQuery(id+"F16.wireOp",EDGE,"E83")}),-1.0]])]});
            var Q5;
            {var subQ0=sQuery(id+"F16.wireOp",EDGE,"E81");var subQ1=sQuery(id+"F16.wireOp",EDGE,"E80");var subQ2=makeQuery(id+"F16.imprint","INTERSECT",VERTEX,{"disambiguationData":[OD(0.0)],"derivedFrom":[subQ1,subQ0]});Q5=makeQuery(id+"F16.imprint","IMPRINT",FACE,{"disambiguationData":[TD([[makeQuery(id+"F16.imprint","IMPRINT",EDGE,{"disambiguationData":[TD([[subQ2,1.0]])],"derivedFrom":subQ1}),1.0]])]});}
            var Q6;
            {var subQ0=sQuery(id+"F16.wireOp",EDGE,"E82");var subQ1=sQuery(id+"F16.wireOp",EDGE,"E80");var subQ2=makeQuery(id+"F16.imprint","INTERSECT",VERTEX,{"disambiguationData":[OD(0.0)],"derivedFrom":[subQ1,subQ0]});Q6=makeQuery(id+"F16.imprint","IMPRINT",FACE,{"disambiguationData":[TD([[makeQuery(id+"F16.imprint","IMPRINT",EDGE,{"disambiguationData":[TD([[subQ2,-1.0]])],"derivedFrom":subQ1}),1.0]])]});}
            extrude(context, id + "F17", {"entities" : qUnion([Q0, Q1, Q2, Q3, Q4, Q5, Q6]), "depth" : 3 * mm});
        }
        {
            var Q0;
            {var subQ0=sQuery(id+"F0.wireOp",EDGE,"E22.filletArc");var subQ1=sQuery(id+"F0.wireOp",EDGE,"E7");var subQ2=sQuery(id+"F0.wireOp",EDGE,"E6");var subQ3=sQuery(id+"F0.wireOp",EDGE,"E5");var subQ4=sQuery(id+"F0.wireOp",EDGE,"E4");var subQ5=sQuery(id+"F0.wireOp",EDGE,"E1.bottom");var subQ6=sQuery(id+"F0.wireOp",EDGE,"E21.filletArc");var subQ7=sQuery(id+"F0.wireOp",EDGE,"E1.top");var subQ8=sQuery(id+"F0.wireOp",EDGE,"E1.left");var subQ9=sQuery(id+"F0.wireOp",EDGE,"E1.right");var subQ10=sQuery(id+"F0.wireOp",EDGE,"E23.filletArc");var subQ11=sQuery(id+"F0.wireOp",EDGE,"E24.filletArc");Q0=makeQuery(id+"F2.boolean.opBoolean","SPLIT",FACE,{"disambiguationData":[TD([makeQuery(id+"F1.opExtrude","SWEPT_FACE",FACE,{"disambiguationData":[OSD([subQ5])]})])],"derivedFrom":makeQuery(id+"F1.opExtrude","CAP_FACE",FACE,{"disambiguationData":[OSD([subQ5,subQ7,subQ8,subQ9,subQ4,subQ3,subQ2,subQ1,subQ6,subQ0,subQ10,subQ11])],"isStart":true})});}
            var sketch = newSketch(context, id + "F18", { "sketchPlane" : qUnion([Q0])});
            skLineSegment(sketch, "E90", {"start": v(0, 74.25) * mm, "end": v(0, 104.31) * mm});
            skCircle(sketch, "E91", {"center": v(0, 104.31) * mm, "radius": 7.58 * mm});
            skCircle(sketch, "E92", {"center": v(0, 104.31) * mm, "radius": 3.06 * mm});
            skLineSegment(sketch, "E93", {"start": v(-7.58, 104.31) * mm, "end": v(-7.58, 86.02) * mm});
            skLineSegment(sketch, "E94", {"start": v(7.58, 104.31) * mm, "end": v(7.58, 86.02) * mm});
            skLineSegment(sketch, "E95", {"start": v(-7.58, 86.02) * mm, "end": v(-7.58, 74.25) * mm});
            skLineSegment(sketch, "E96", {"start": v(-7.58, 74.25) * mm, "end": v(7.58, 74.25) * mm});
            skLineSegment(sketch, "E97", {"start": v(7.58, 74.25) * mm, "end": v(7.58, 86.02) * mm});
            skLineSegment(sketch, "E98", {"start": v(-7.58, 86.02) * mm, "end": v(-19.46, 74.25) * mm});
            skLineSegment(sketch, "E99", {"start": v(-19.46, 74.25) * mm, "end": v(22.15, 74.25) * mm});
            skLineSegment(sketch, "E100", {"start": v(22.15, 74.25) * mm, "end": v(7.58, 86.02) * mm});
            skSolve(sketch);
        }
        {
            var Q0;
            {var subQ0=sQuery(id+"F18.wireOp",EDGE,"E95");Q0=makeQuery(id+"F18.imprint","IMPRINT",FACE,{"disambiguationData":[TD([[makeQuery(id+"F18.imprint","IMPRINT",EDGE,{"derivedFrom":subQ0}),-1.0]])]});}
            var Q1;
            {var subQ0=sQuery(id+"F18.wireOp",EDGE,"E97");Q1=makeQuery(id+"F18.imprint","IMPRINT",FACE,{"disambiguationData":[TD([[makeQuery(id+"F18.imprint","IMPRINT",EDGE,{"derivedFrom":subQ0}),-1.0]])]});}
            var Q2;
            Q2=makeQuery(id+"F18.imprint","IMPRINT",FACE,{"disambiguationData":[TD([[makeQuery(id+"F18.imprint","IMPRINT",EDGE,{"derivedFrom":sQuery(id+"F18.wireOp",EDGE,"E92")}),-1.0]])]});
            var Q3;
            {var subQ1=sQuery(id+"F18.wireOp",EDGE,"E93");Q3=makeQuery(id+"F18.imprint","IMPRINT",FACE,{"disambiguationData":[TD([[makeQuery(id+"F18.imprint","IMPRINT",EDGE,{"derivedFrom":subQ1}),1.0]])]});}
            var Q4;
            {var subQ0=sQuery(id+"F18.wireOp",EDGE,"E94");Q4=makeQuery(id+"F18.imprint","IMPRINT",FACE,{"disambiguationData":[TD([[makeQuery(id+"F18.imprint","IMPRINT",EDGE,{"derivedFrom":subQ0}),-1.0]])]});}
            extrude(context, id + "F19", {"entities" : qUnion([Q0, Q1, Q2, Q3, Q4]), "depth" : 3 * mm});
        }
        {
            var Q0;
            {var subQ0=sQuery(id+"F0.wireOp",EDGE,"E22.filletArc");var subQ1=sQuery(id+"F0.wireOp",EDGE,"E7");var subQ2=sQuery(id+"F0.wireOp",EDGE,"E6");var subQ3=sQuery(id+"F0.wireOp",EDGE,"E5");var subQ4=sQuery(id+"F0.wireOp",EDGE,"E4");var subQ5=sQuery(id+"F0.wireOp",EDGE,"E1.bottom");var subQ6=sQuery(id+"F0.wireOp",EDGE,"E21.filletArc");var subQ7=sQuery(id+"F0.wireOp",EDGE,"E1.top");var subQ8=sQuery(id+"F0.wireOp",EDGE,"E1.left");var subQ9=sQuery(id+"F0.wireOp",EDGE,"E1.right");var subQ10=sQuery(id+"F0.wireOp",EDGE,"E23.filletArc");var subQ11=sQuery(id+"F0.wireOp",EDGE,"E24.filletArc");Q0=makeQuery(id+"F2.boolean.opBoolean","SPLIT",FACE,{"disambiguationData":[TD([makeQuery(id+"F1.opExtrude","SWEPT_FACE",FACE,{"disambiguationData":[OSD([subQ5])]})])],"derivedFrom":makeQuery(id+"F1.opExtrude","CAP_FACE",FACE,{"disambiguationData":[OSD([subQ5,subQ7,subQ8,subQ9,subQ4,subQ3,subQ2,subQ1,subQ6,subQ0,subQ10,subQ11])],"isStart":true})});}
            var sketch = newSketch(context, id + "F20", { "sketchPlane" : qUnion([Q0])});
            skLineSegment(sketch, "E101", {"start": v(-64.25, 74.25) * mm, "end": v(64.25, 74.25) * mm});
            skLineSegment(sketch, "E102", {"start": v(74.25, 64.25) * mm, "end": v(74.25, -64.25) * mm});
            skLineSegment(sketch, "E103", {"start": v(64.25, -74.25) * mm, "end": v(-64.25, -74.25) * mm});
            skLineSegment(sketch, "E104", {"start": v(-60, 38.83) * mm, "end": v(-60, -38.83) * mm});
            skArc(sketch, "E105", {"start": v(60, 38.83) * mm, "mid": v(58.44, 44.2) * mm, "end": v(54.26, 47.88) * mm});
            skArc(sketch, "E106", {"start": v(54.26, 47.88) * mm, "mid": v(0, 60.05) * mm, "end": v(-54.26, 47.88) * mm});
            skArc(sketch, "E107", {"start": v(-54.26, 47.88) * mm, "mid": v(-58.44, 44.2) * mm, "end": v(-60, 38.83) * mm});
            skArc(sketch, "E108", {"start": v(-60, -38.83) * mm, "mid": v(-58.44, -44.2) * mm, "end": v(-54.26, -47.88) * mm});
            skArc(sketch, "E109", {"start": v(-54.26, -47.88) * mm, "mid": v(0, -59.89) * mm, "end": v(54.26, -47.88) * mm});
            skArc(sketch, "E110", {"start": v(54.26, -47.88) * mm, "mid": v(58.44, -44.2) * mm, "end": v(60, -38.83) * mm});
            skLineSegment(sketch, "E111", {"start": v(60, 38.83) * mm, "end": v(60, -38.83) * mm});
            skArc(sketch, "E112", {"start": v(-74.25, -64.25) * mm, "mid": v(-71.32, -71.32) * mm, "end": v(-64.25, -74.25) * mm});
            skLineSegment(sketch, "E113", {"start": v(-74.25, -64.25) * mm, "end": v(-74.25, 64.25) * mm});
            skArc(sketch, "E114", {"start": v(-64.25, 74.25) * mm, "mid": v(-71.32, 71.32) * mm, "end": v(-74.25, 64.25) * mm});
            skArc(sketch, "E115", {"start": v(74.25, 64.25) * mm, "mid": v(71.32, 71.32) * mm, "end": v(64.25, 74.25) * mm});
            skArc(sketch, "E116", {"start": v(64.25, -74.25) * mm, "mid": v(71.32, -71.32) * mm, "end": v(74.25, -64.25) * mm});
            skCircle(sketch, "E117", {"center": v(-60, -60) * mm, "radius": 3.86 * mm});
            skCircle(sketch, "E118", {"center": v(60, -60) * mm, "radius": 3.97 * mm});
            skCircle(sketch, "E119", {"center": v(60, 60) * mm, "radius": 3.9 * mm});
            skCircle(sketch, "E120", {"center": v(-60, 60) * mm, "radius": 4.01 * mm});
            skSolve(sketch);
        }
        {
            var Q0;
            Q0 = qSketchRegion(id + "F20", true);
            extrude(context, id + "F21", {"entities" : qUnion([Q0]), "oppositeDirection" : true, "depth" : 3 * mm});
        }
        {
            var Q0;
            Q0 = qSketchRegion(id + "F20", true);
            extrude(context, id + "F22", {"entities" : qUnion([Q0]), "depth" : 3 * mm});
        }
    });
